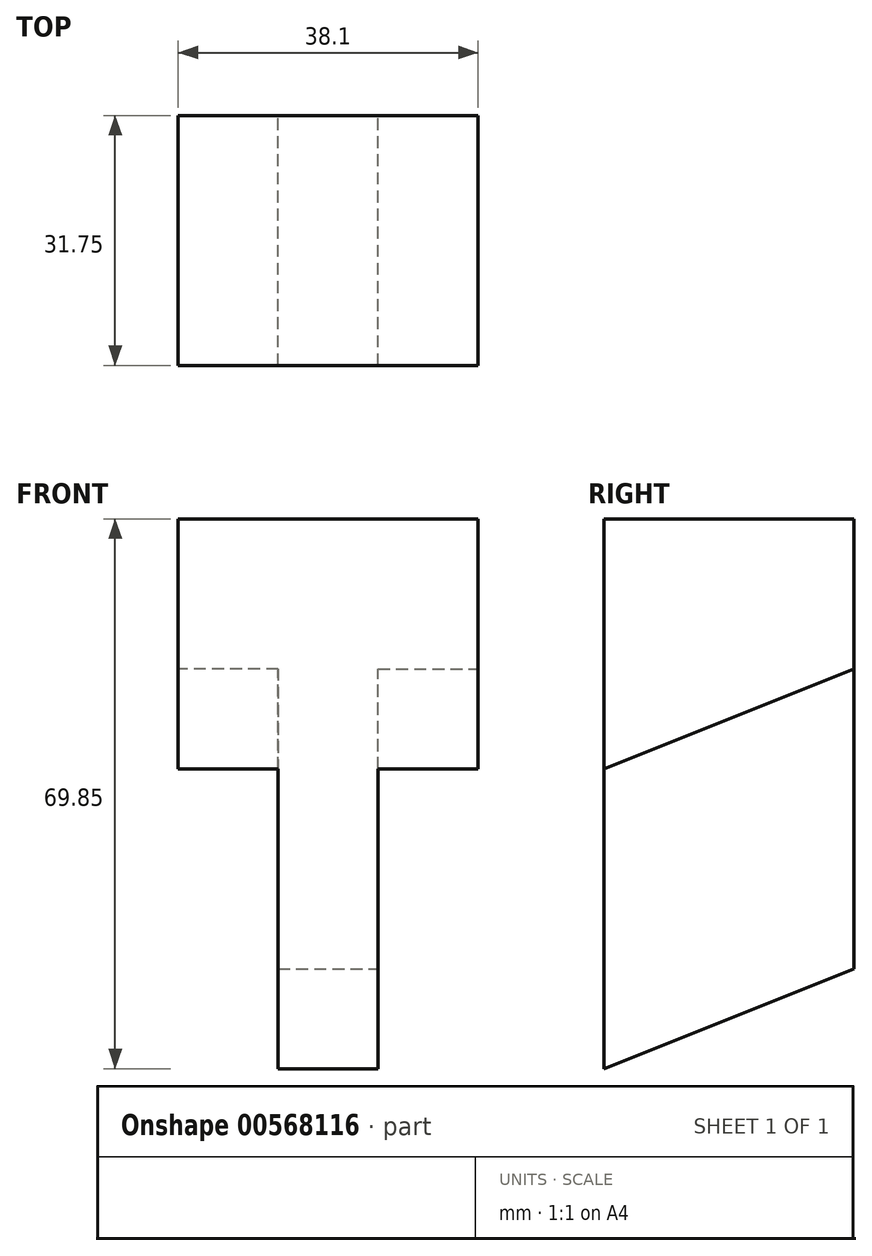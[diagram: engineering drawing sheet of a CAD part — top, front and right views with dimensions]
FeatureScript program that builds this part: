
annotation { "Feature Type Name" : "Feature", "Feature Type Description" : "" }
export const myFeature = defineFeature(function(context is Context, id is Id, definition is map)
    precondition{}
    {
        {
            var Q0;
            Q0=qCreatedBy(makeId("Front.planeOp"),FACE);
            var sketch = newSketch(context, id + "F0", { "sketchPlane" : qUnion([Q0])});
            skLineSegment(sketch, "E0", {"start": v(-57.27, 59.01) * mm, "end": v(-57.27, 27.26) * mm});
            skLineSegment(sketch, "E1", {"start": v(-57.27, 27.26) * mm, "end": v(-44.57, 27.26) * mm});
            skLineSegment(sketch, "E2", {"start": v(-44.57, 27.26) * mm, "end": v(-44.57, -10.84) * mm});
            skLineSegment(sketch, "E3", {"start": v(-44.57, -10.84) * mm, "end": v(-31.87, -10.84) * mm});
            skLineSegment(sketch, "E4", {"start": v(-31.87, -10.84) * mm, "end": v(-31.87, 27.26) * mm});
            skLineSegment(sketch, "E5", {"start": v(-31.87, 27.26) * mm, "end": v(-19.17, 27.26) * mm});
            skLineSegment(sketch, "E6", {"start": v(-19.17, 27.26) * mm, "end": v(-19.17, 59.01) * mm});
            skLineSegment(sketch, "E7", {"start": v(-19.17, 59.01) * mm, "end": v(-57.27, 59.01) * mm});
            skSolve(sketch);
        }
        {
            var Q0;
            Q0 = qSketchRegion(id + "F0", true);
            extrude(context, id + "F1", {"entities" : qUnion([Q0]), "depth" : 31.75 * mm, "offsetDistance" : 25.4 * mm});
        }
        {
            var Q0;
            Q0=makeQuery(id+"F1.opExtrude","SWEPT_FACE",FACE,{"disambiguationData":[OSD([sQuery(id+"F0.wireOp",EDGE,"E4")])]});
            var sketch = newSketch(context, id + "F2", { "sketchPlane" : qUnion([Q0])});
            skLineSegment(sketch, "E8", {"start": v(-31.75, -10.84) * mm, "end": v(0, 1.86) * mm});
            skSolve(sketch);
        }
        {
            var Q0;
            {var subQ0=sQuery(id+"F2.wireOp",EDGE,"E8");Q0=makeQuery(id+"F2.imprint","IMPRINT",FACE,{"disambiguationData":[TD([[makeQuery(id+"F2.imprint","IMPRINT",EDGE,{"derivedFrom":subQ0}),-1.0]])]});}
            extrude(context, id + "F3", {"entities" : qUnion([Q0]), "operationType" : NewBodyOperationType.REMOVE, "oppositeDirection" : true, "depth" : 25.4 * mm, "offsetDistance" : 25.4 * mm});
        }
        {
            var Q0;
            Q0=makeQuery(id+"F1.opExtrude","SWEPT_FACE",FACE,{"disambiguationData":[OSD([sQuery(id+"F0.wireOp",EDGE,"E6")])]});
            var sketch = newSketch(context, id + "F4", { "sketchPlane" : qUnion([Q0])});
            skLineSegment(sketch, "E9", {"start": v(-31.75, 27.26) * mm, "end": v(0, 39.96) * mm});
            skSolve(sketch);
        }
        {
            var Q0;
            {var subQ0=sQuery(id+"F4.wireOp",EDGE,"E9");Q0=makeQuery(id+"F4.imprint","IMPRINT",FACE,{"disambiguationData":[TD([[makeQuery(id+"F4.imprint","IMPRINT",EDGE,{"derivedFrom":subQ0}),-1.0]])]});}
            extrude(context, id + "F5", {"entities" : qUnion([Q0]), "operationType" : NewBodyOperationType.REMOVE, "oppositeDirection" : true, "depth" : 12.7 * mm, "offsetDistance" : 25.4 * mm});
        }
        {
            var Q0;
            Q0=makeQuery(id+"F1.opExtrude","SWEPT_FACE",FACE,{"disambiguationData":[OSD([sQuery(id+"F0.wireOp",EDGE,"E0")])]});
            var sketch = newSketch(context, id + "F6", { "sketchPlane" : qUnion([Q0])});
            skLineSegment(sketch, "E10", {"start": v(31.75, 27.26) * mm, "end": v(0, 39.96) * mm});
            skSolve(sketch);
        }
        {
            var Q0;
            {var subQ0=sQuery(id+"F6.wireOp",EDGE,"E10");Q0=makeQuery(id+"F6.imprint","IMPRINT",FACE,{"disambiguationData":[TD([[makeQuery(id+"F6.imprint","IMPRINT",EDGE,{"derivedFrom":subQ0}),1.0]])]});}
            extrude(context, id + "F7", {"entities" : qUnion([Q0]), "operationType" : NewBodyOperationType.REMOVE, "oppositeDirection" : true, "depth" : 12.7 * mm, "offsetDistance" : 25.4 * mm});
        }
    });
